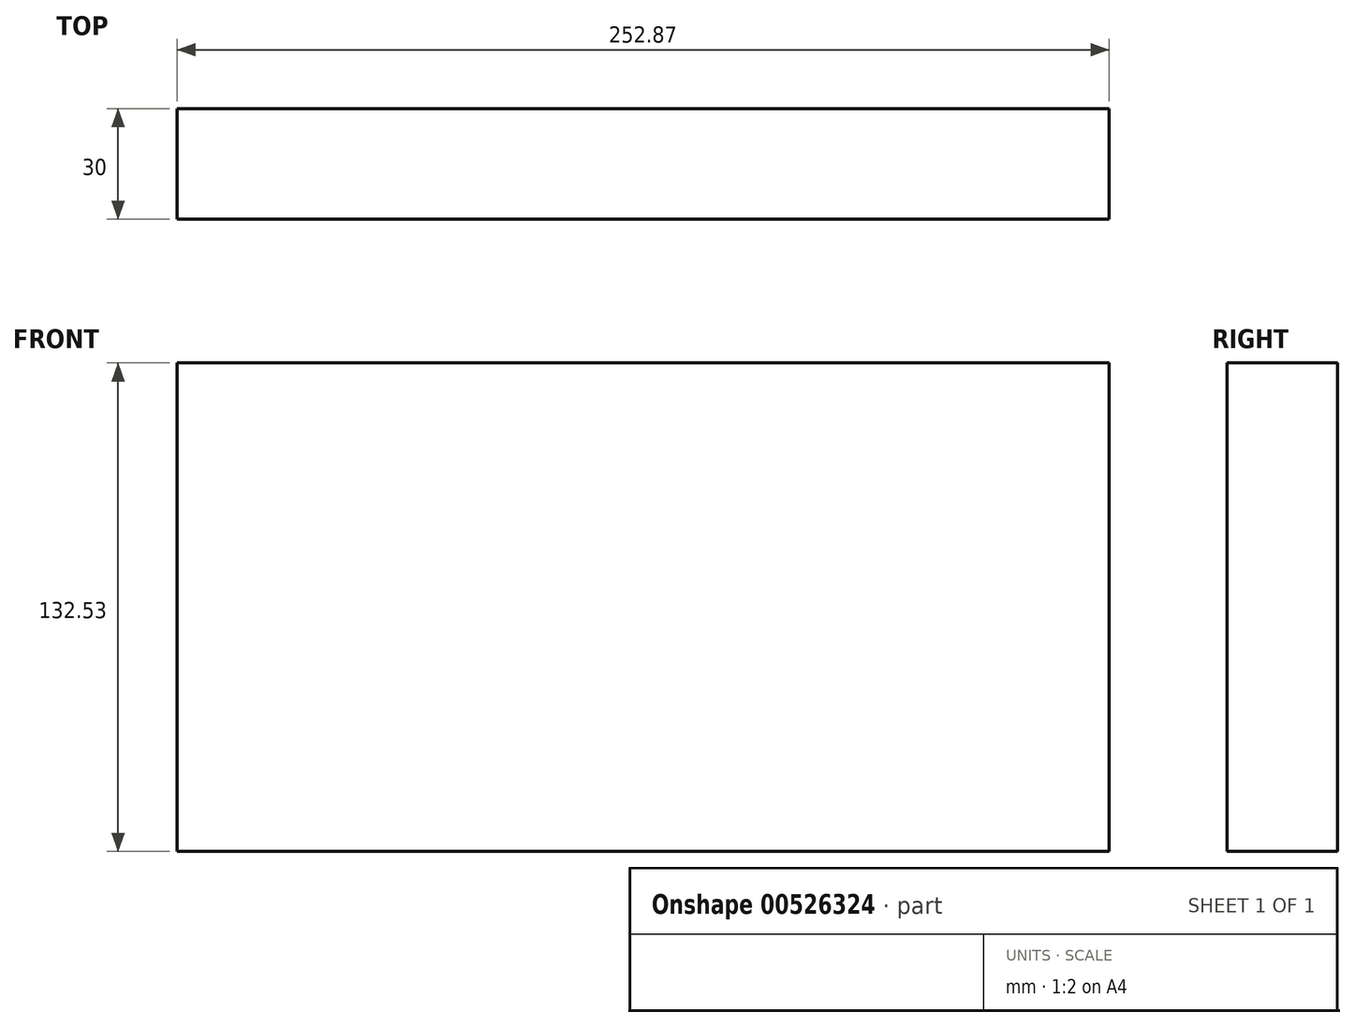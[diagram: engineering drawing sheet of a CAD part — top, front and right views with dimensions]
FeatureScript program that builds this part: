
annotation { "Feature Type Name" : "Feature", "Feature Type Description" : "" }
export const myFeature = defineFeature(function(context is Context, id is Id, definition is map)
    precondition{}
    {
        {
            var Q0;
            Q0=qCreatedBy(makeId("Front.planeOp"),FACE);
            var sketch = newSketch(context, id + "F0", { "sketchPlane" : qUnion([Q0])});
            skLineSegment(sketch, "E0.bottom", {"start": v(-146.34, 57.29) * mm, "end": v(106.53, 57.29) * mm});
            skLineSegment(sketch, "E0.top", {"start": v(-146.34, -75.24) * mm, "end": v(106.53, -75.24) * mm});
            skLineSegment(sketch, "E0.left", {"start": v(-146.34, 57.29) * mm, "end": v(-146.34, -75.24) * mm});
            skLineSegment(sketch, "E0.right", {"start": v(106.53, 57.29) * mm, "end": v(106.53, -75.24) * mm});
            skSolve(sketch);
        }
        {
            var Q0;
            Q0=makeQuery(id+"F0.imprint","IMPRINT",FACE,{"disambiguationData":[TD([[makeQuery(id+"F0.imprint","IMPRINT",EDGE,{"derivedFrom":sQuery(id+"F0.wireOp",EDGE,"E0.bottom")}),-1.0]])]});
            extrude(context, id + "F1", {"entities" : qUnion([Q0]), "depth" : 30 * mm, "offsetDistance" : 25.4 * mm});
        }
    });
